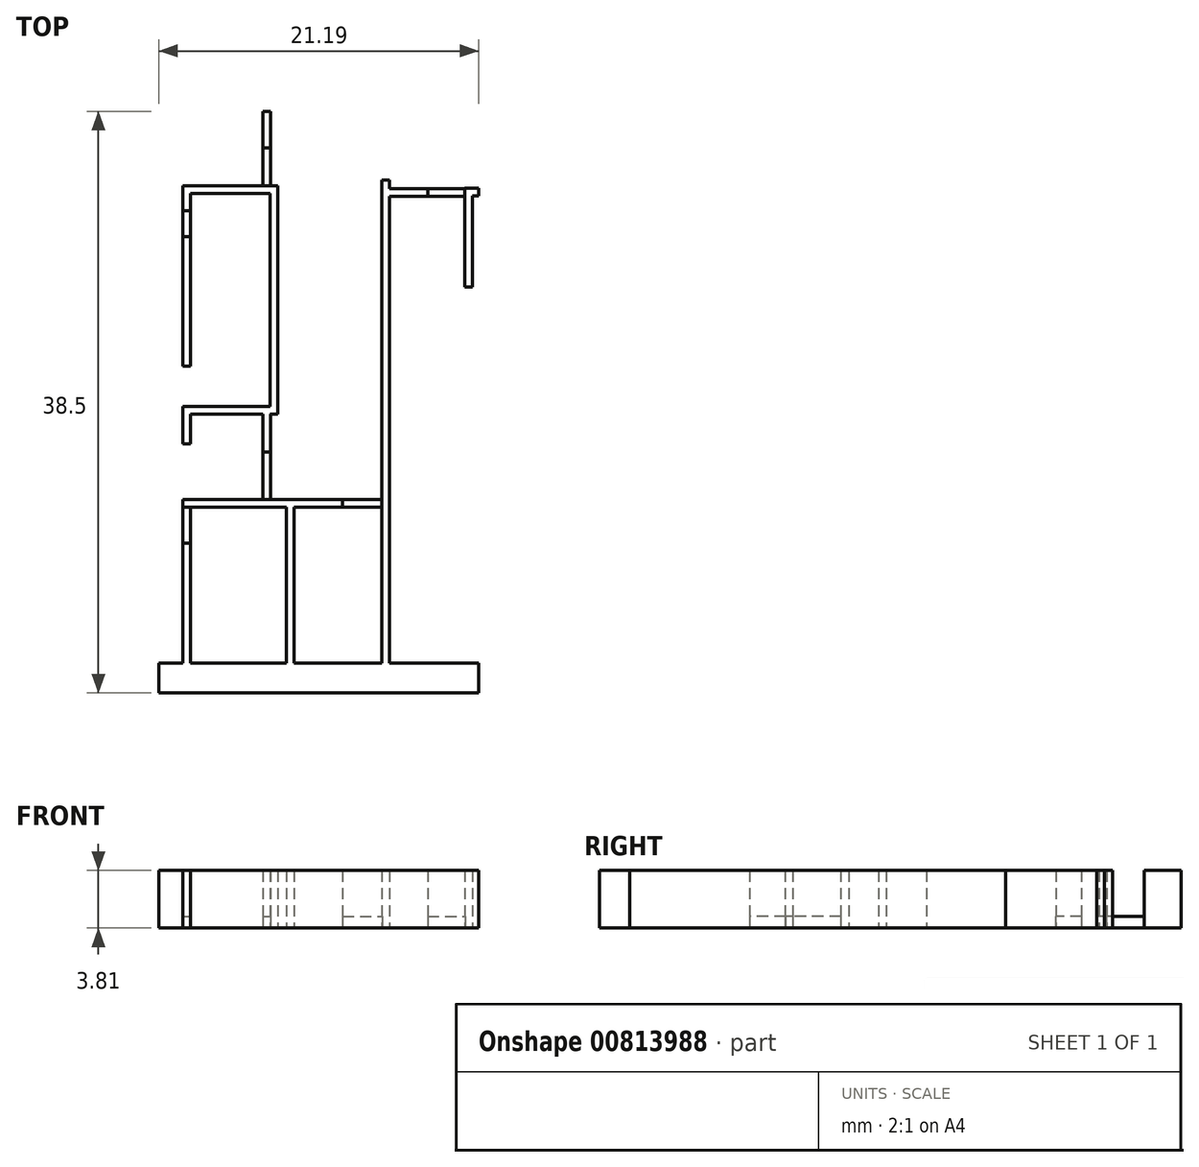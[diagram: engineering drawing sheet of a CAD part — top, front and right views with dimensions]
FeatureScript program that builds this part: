
annotation { "Feature Type Name" : "Feature", "Feature Type Description" : "" }
export const myFeature = defineFeature(function(context is Context, id is Id, definition is map)
    precondition{}
    {
        {
            var Q0;
            Q0=qCreatedBy(makeId("Top.planeOp"),FACE);
            var sketch = newSketch(context, id + "F0", { "sketchPlane" : qUnion([Q0])});
            skLineSegment(sketch, "E0.top", {"start": v(-48.09, -40.14) * mm, "end": v(-47.58, -40.14) * mm});
            skLineSegment(sketch, "E0.left", {"start": v(-48.09, -37.7) * mm, "end": v(-48.09, -40.14) * mm});
            skLineSegment(sketch, "E0.right", {"start": v(-47.58, -37.7) * mm, "end": v(-47.58, -40.14) * mm});
            skLineSegment(sketch, "E1.bottom", {"start": v(-53.37, -46) * mm, "end": v(-52.86, -46) * mm});
            skLineSegment(sketch, "E1.top", {"start": v(-53.37, -54.56) * mm, "end": v(-52.86, -54.56) * mm});
            skLineSegment(sketch, "E1.left", {"start": v(-53.37, -46) * mm, "end": v(-53.37, -54.56) * mm});
            skLineSegment(sketch, "E1.right", {"start": v(-52.86, -46) * mm, "end": v(-52.86, -54.56) * mm});
            skLineSegment(sketch, "E2.bottom", {"start": v(-47.1, -42.63) * mm, "end": v(-47.6, -42.63) * mm});
            skLineSegment(sketch, "E2.top", {"start": v(-47.1, -57.75) * mm, "end": v(-47.6, -57.75) * mm});
            skLineSegment(sketch, "E2.left", {"start": v(-47.1, -42.63) * mm, "end": v(-47.1, -57.75) * mm});
            skLineSegment(sketch, "E2.right", {"start": v(-47.6, -42.63) * mm, "end": v(-47.6, -57.75) * mm});
            skLineSegment(sketch, "E3.bottom", {"start": v(-47.6, -42.63) * mm, "end": v(-53.37, -42.63) * mm});
            skLineSegment(sketch, "E3.top", {"start": v(-47.6, -43.14) * mm, "end": v(-53.37, -43.14) * mm});
            skLineSegment(sketch, "E3.left", {"start": v(-47.6, -42.63) * mm, "end": v(-47.6, -43.14) * mm});
            skLineSegment(sketch, "E3.right", {"start": v(-53.37, -42.63) * mm, "end": v(-53.37, -43.14) * mm});
            skLineSegment(sketch, "E4.bottom", {"start": v(-47.6, -57.24) * mm, "end": v(-53.37, -57.24) * mm});
            skLineSegment(sketch, "E4.top", {"start": v(-47.6, -57.75) * mm, "end": v(-53.37, -57.75) * mm});
            skLineSegment(sketch, "E4.left", {"start": v(-47.6, -57.24) * mm, "end": v(-47.6, -57.75) * mm});
            skLineSegment(sketch, "E4.right", {"start": v(-53.37, -57.24) * mm, "end": v(-53.37, -57.75) * mm});
            skLineSegment(sketch, "E5.bottom", {"start": v(-53.37, -43.14) * mm, "end": v(-52.86, -43.14) * mm});
            skLineSegment(sketch, "E5.top", {"start": v(-53.37, -44.29) * mm, "end": v(-52.86, -44.29) * mm});
            skLineSegment(sketch, "E5.left", {"start": v(-53.37, -43.14) * mm, "end": v(-53.37, -44.29) * mm});
            skLineSegment(sketch, "E5.right", {"start": v(-52.86, -43.14) * mm, "end": v(-52.86, -44.29) * mm});
            skLineSegment(sketch, "E6.bottom", {"start": v(-53.37, -57.75) * mm, "end": v(-52.86, -57.75) * mm});
            skLineSegment(sketch, "E6.top", {"start": v(-53.37, -59.71) * mm, "end": v(-52.86, -59.71) * mm});
            skLineSegment(sketch, "E6.left", {"start": v(-53.37, -57.75) * mm, "end": v(-53.37, -59.71) * mm});
            skLineSegment(sketch, "E6.right", {"start": v(-52.86, -57.75) * mm, "end": v(-52.86, -59.71) * mm});
            skLineSegment(sketch, "E7.bottom", {"start": v(-48.09, -60.24) * mm, "end": v(-47.58, -60.24) * mm});
            skLineSegment(sketch, "E7.top", {"start": v(-48.09, -57.75) * mm, "end": v(-47.58, -57.75) * mm});
            skLineSegment(sketch, "E7.left", {"start": v(-48.09, -60.24) * mm, "end": v(-48.09, -57.75) * mm});
            skLineSegment(sketch, "E7.right", {"start": v(-47.58, -60.24) * mm, "end": v(-47.58, -57.75) * mm});
            skLineSegment(sketch, "E8.bottom", {"start": v(-53.37, -66.27) * mm, "end": v(-52.86, -66.27) * mm});
            skLineSegment(sketch, "E8.top", {"start": v(-53.37, -76.2) * mm, "end": v(-52.53, -76.2) * mm});
            skLineSegment(sketch, "E8.left", {"start": v(-53.37, -66.27) * mm, "end": v(-53.37, -76.2) * mm});
            skLineSegment(sketch, "E8.right", {"start": v(-52.86, -66.27) * mm, "end": v(-52.86, -76.2) * mm});
            skLineSegment(sketch, "E9.bottom", {"start": v(-42.8, -63.4) * mm, "end": v(-53.37, -63.4) * mm});
            skLineSegment(sketch, "E9.top", {"start": v(-42.8, -63.9) * mm, "end": v(-53.37, -63.9) * mm});
            skLineSegment(sketch, "E9.left", {"start": v(-42.8, -63.4) * mm, "end": v(-42.8, -63.9) * mm});
            skLineSegment(sketch, "E9.right", {"start": v(-53.37, -63.4) * mm, "end": v(-53.37, -63.9) * mm});
            skLineSegment(sketch, "E10.bottom", {"start": v(-46, -63.9) * mm, "end": v(-46.51, -63.9) * mm});
            skLineSegment(sketch, "E10.top", {"start": v(-46, -76.16) * mm, "end": v(-46.51, -76.16) * mm});
            skLineSegment(sketch, "E10.left", {"start": v(-46, -63.9) * mm, "end": v(-46, -76.16) * mm});
            skLineSegment(sketch, "E10.right", {"start": v(-46.51, -63.9) * mm, "end": v(-46.51, -76.16) * mm});
            skLineSegment(sketch, "E11.bottom", {"start": v(-33.78, -43.28) * mm, "end": v(-34.7, -43.28) * mm});
            skLineSegment(sketch, "E11.top", {"start": v(-33.78, -42.78) * mm, "end": v(-34.7, -42.78) * mm});
            skLineSegment(sketch, "E11.right", {"start": v(-34.7, -43.28) * mm, "end": v(-34.7, -42.78) * mm});
            skLineSegment(sketch, "E12.bottom", {"start": v(-34.7, -43.28) * mm, "end": v(-34.2, -43.28) * mm});
            skLineSegment(sketch, "E12.top", {"start": v(-34.7, -49.31) * mm, "end": v(-34.2, -49.31) * mm});
            skLineSegment(sketch, "E12.left", {"start": v(-34.7, -43.28) * mm, "end": v(-34.7, -49.31) * mm});
            skLineSegment(sketch, "E12.right", {"start": v(-34.2, -43.28) * mm, "end": v(-34.2, -49.31) * mm});
            skLineSegment(sketch, "E13.bottom", {"start": v(-40.2, -42.24) * mm, "end": v(-39.7, -42.24) * mm});
            skLineSegment(sketch, "E13.top", {"start": v(-40.2, -76.18) * mm, "end": v(-39.7, -76.18) * mm});
            skLineSegment(sketch, "E13.left", {"start": v(-40.2, -42.24) * mm, "end": v(-40.2, -76.18) * mm});
            skLineSegment(sketch, "E13.right", {"start": v(-39.7, -42.24) * mm, "end": v(-39.7, -76.18) * mm});
            skLineSegment(sketch, "E14", {"start": v(-54.97, -76.87) * mm, "end": v(-54.97, -37.7) * mm});
            skLineSegment(sketch, "E15", {"start": v(-54.97, -37.7) * mm, "end": v(-33.79, -37.7) * mm});
            skLineSegment(sketch, "E16", {"start": v(-33.79, -37.7) * mm, "end": v(-33.79, -76.11) * mm});
            skLineSegment(sketch, "E17", {"start": v(-48.09, -37.7) * mm, "end": v(-47.58, -37.7) * mm});
            skLineSegment(sketch, "E18", {"start": v(-33.78, -42.78) * mm, "end": v(-33.78, -43.28) * mm});
            skLineSegment(sketch, "E19.bottom", {"start": v(-54.97, -74.22) * mm, "end": v(-33.79, -74.22) * mm});
            skLineSegment(sketch, "E19.top", {"start": v(-54.97, -76.2) * mm, "end": v(-33.79, -76.2) * mm});
            skLineSegment(sketch, "E19.left", {"start": v(-54.97, -74.22) * mm, "end": v(-54.97, -76.2) * mm});
            skLineSegment(sketch, "E19.right", {"start": v(-33.79, -74.22) * mm, "end": v(-33.79, -76.2) * mm});
            skLineSegment(sketch, "E20.bottom", {"start": v(-39.7, -42.83) * mm, "end": v(-37.16, -42.83) * mm});
            skLineSegment(sketch, "E20.top", {"start": v(-39.7, -43.34) * mm, "end": v(-37.16, -43.34) * mm});
            skLineSegment(sketch, "E20.left", {"start": v(-39.7, -42.83) * mm, "end": v(-39.7, -43.34) * mm});
            skLineSegment(sketch, "E20.right", {"start": v(-37.16, -42.83) * mm, "end": v(-37.16, -43.34) * mm});
            skSolve(sketch);
        }
        {
            var Q0;
            Q0 = qSketchRegion(id + "F0", true);
            extrude(context, id + "F1", {"entities" : qUnion([Q0]), "depth" : 3.8 * mm, "offsetDistance" : 25.4 * mm});
        }
        {
            var Q0;
            Q0=qCreatedBy(makeId("Top.planeOp"),FACE);
            var sketch = newSketch(context, id + "F2", { "sketchPlane" : qUnion([Q0])});
            skLineSegment(sketch, "E21.bottom", {"start": v(-48.09, -60.24) * mm, "end": v(-47.58, -60.24) * mm});
            skLineSegment(sketch, "E21.top", {"start": v(-48.09, -63.43) * mm, "end": v(-47.58, -63.43) * mm});
            skLineSegment(sketch, "E21.left", {"start": v(-48.09, -60.24) * mm, "end": v(-48.09, -63.43) * mm});
            skLineSegment(sketch, "E21.right", {"start": v(-47.58, -60.24) * mm, "end": v(-47.58, -63.43) * mm});
            skLineSegment(sketch, "E22.bottom", {"start": v(-53.37, -63.88) * mm, "end": v(-52.86, -63.88) * mm});
            skLineSegment(sketch, "E22.top", {"start": v(-53.37, -66.27) * mm, "end": v(-52.86, -66.27) * mm});
            skLineSegment(sketch, "E22.left", {"start": v(-53.37, -63.88) * mm, "end": v(-53.37, -66.27) * mm});
            skLineSegment(sketch, "E22.right", {"start": v(-52.86, -63.88) * mm, "end": v(-52.86, -66.27) * mm});
            skLineSegment(sketch, "E23.bottom", {"start": v(-42.8, -63.4) * mm, "end": v(-40.18, -63.4) * mm});
            skLineSegment(sketch, "E23.top", {"start": v(-42.8, -63.91) * mm, "end": v(-40.18, -63.91) * mm});
            skLineSegment(sketch, "E23.left", {"start": v(-42.8, -63.4) * mm, "end": v(-42.8, -63.91) * mm});
            skLineSegment(sketch, "E23.right", {"start": v(-40.18, -63.4) * mm, "end": v(-40.18, -63.91) * mm});
            skLineSegment(sketch, "E24.bottom", {"start": v(-37.16, -42.83) * mm, "end": v(-34.68, -42.83) * mm});
            skLineSegment(sketch, "E24.top", {"start": v(-37.16, -43.34) * mm, "end": v(-34.68, -43.34) * mm});
            skLineSegment(sketch, "E24.left", {"start": v(-37.16, -42.83) * mm, "end": v(-37.16, -43.34) * mm});
            skLineSegment(sketch, "E24.right", {"start": v(-34.68, -42.83) * mm, "end": v(-34.68, -43.34) * mm});
            skLineSegment(sketch, "E25.bottom", {"start": v(-53.37, -44.29) * mm, "end": v(-52.86, -44.29) * mm});
            skLineSegment(sketch, "E25.top", {"start": v(-53.37, -46.02) * mm, "end": v(-52.86, -46.02) * mm});
            skLineSegment(sketch, "E25.left", {"start": v(-53.37, -44.29) * mm, "end": v(-53.37, -46.02) * mm});
            skLineSegment(sketch, "E25.right", {"start": v(-52.86, -44.29) * mm, "end": v(-52.86, -46.02) * mm});
            skLineSegment(sketch, "E26.bottom", {"start": v(-48.09, -40.14) * mm, "end": v(-47.58, -40.14) * mm});
            skLineSegment(sketch, "E26.top", {"start": v(-48.09, -42.66) * mm, "end": v(-47.58, -42.66) * mm});
            skLineSegment(sketch, "E26.left", {"start": v(-48.09, -40.14) * mm, "end": v(-48.09, -42.66) * mm});
            skLineSegment(sketch, "E26.right", {"start": v(-47.58, -40.14) * mm, "end": v(-47.58, -42.66) * mm});
            skSolve(sketch);
        }
        {
            var Q0;
            Q0 = qSketchRegion(id + "F2", true);
            extrude(context, id + "F3", {"entities" : qUnion([Q0]), "depth" : 0.76 * mm, "offsetDistance" : 25.4 * mm});
        }
    });
